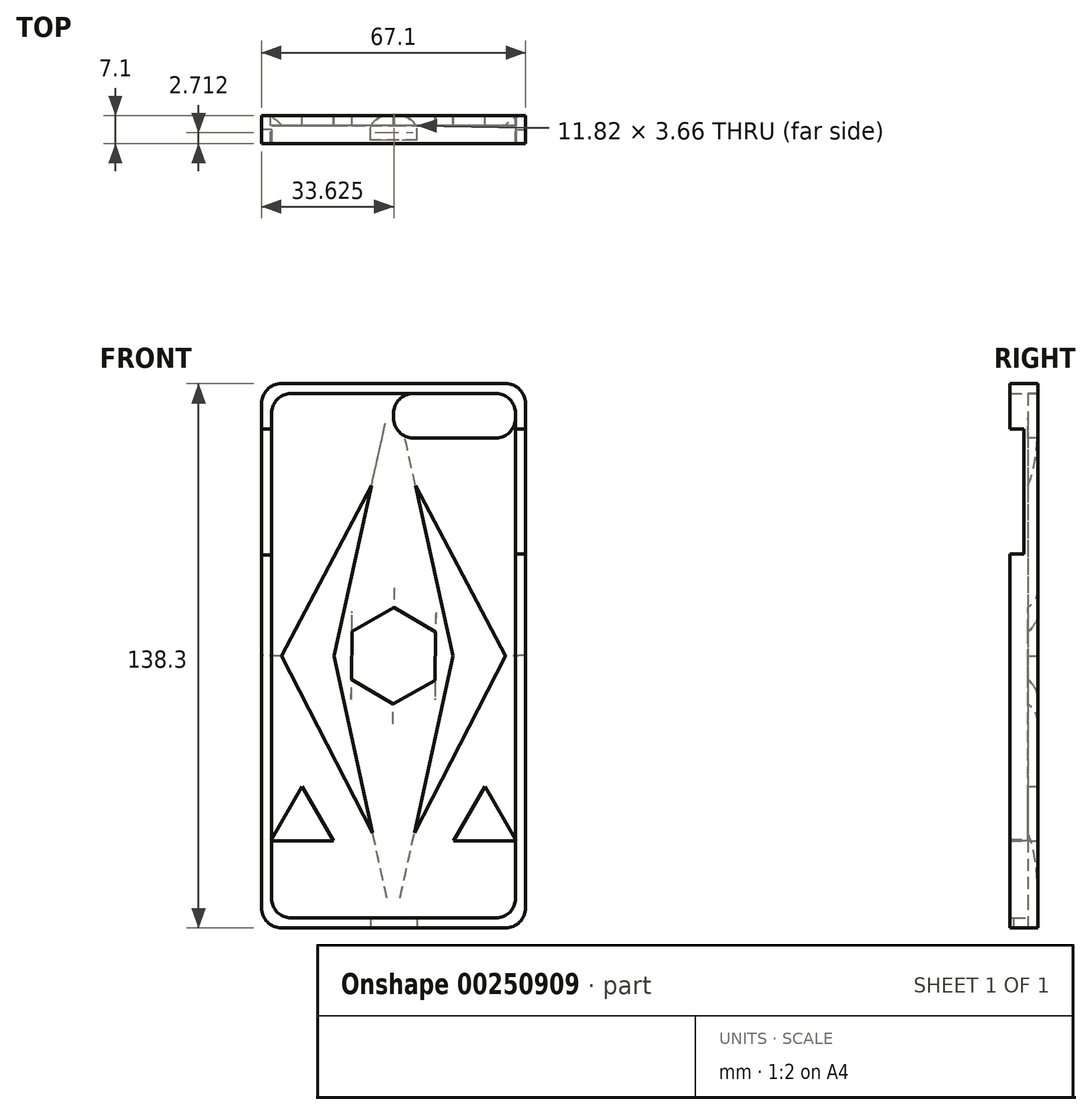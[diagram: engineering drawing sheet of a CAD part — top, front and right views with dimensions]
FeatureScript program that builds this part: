
annotation { "Feature Type Name" : "Feature", "Feature Type Description" : "" }
export const myFeature = defineFeature(function(context is Context, id is Id, definition is map)
    precondition{}
    {
        {
            var Q0;
            Q0=qCreatedBy(makeId("Front.planeOp"),FACE);
            var sketch = newSketch(context, id + "F0", { "sketchPlane" : qUnion([Q0])});
            skLineSegment(sketch, "E0.bottom", {"start": v(33.55, 69.15) * mm, "end": v(-33.55, 69.15) * mm});
            skLineSegment(sketch, "E0.top", {"start": v(33.55, -69.15) * mm, "end": v(-33.55, -69.15) * mm});
            skLineSegment(sketch, "E0.left", {"start": v(33.55, 69.15) * mm, "end": v(33.55, -69.15) * mm});
            skLineSegment(sketch, "E0.right", {"start": v(-33.55, 69.15) * mm, "end": v(-33.55, -69.15) * mm});
            skPoint(sketch, "E0.middle", {"position": v(0, 0) * mm});
            skSolve(sketch);
        }
        {
            var Q0;
            Q0=makeQuery(id+"F0.imprint","IMPRINT",FACE,{"disambiguationData":[TD([[makeQuery(id+"F0.imprint","IMPRINT",EDGE,{"derivedFrom":sQuery(id+"F0.wireOp",EDGE,"E0.bottom")}),1.0]])]});
            var Q1;
            Q1=sQuery(id+"F0.wireOp",EDGE,"E0.bottom");
            extrude(context, id + "F1", {"entities" : qUnion([Q0]), "surfaceEntities" : qUnion([Q1]), "endBound" : BoundingType.SYMMETRIC, "depth" : 7.1 * mm});
        }
        {
            var Q0;
            Q0=makeQuery(id+"F1.opExtrude","CAP_FACE",FACE,{"disambiguationData":[OSD([sQuery(id+"F0.wireOp",EDGE,"E0.bottom"),sQuery(id+"F0.wireOp",EDGE,"E0.top"),sQuery(id+"F0.wireOp",EDGE,"E0.left"),sQuery(id+"F0.wireOp",EDGE,"E0.right")])],"isStart":false});
            var Q1;
            Q1=makeQuery(id+"F1.opExtrude","SWEPT_BODY",BODY,{"disambiguationData":[OSD([sQuery(id+"F0.wireOp",EDGE,"E0.bottom"),sQuery(id+"F0.wireOp",EDGE,"E0.top"),sQuery(id+"F0.wireOp",EDGE,"E0.left"),sQuery(id+"F0.wireOp",EDGE,"E0.right")])]});
            shell(context, id + "F2", {"entities" : qUnion([Q0]), "parts" : qUnion([Q1]), "thickness" : 2.54 * mm});
        }
        {
            var Q0;
            Q0=makeQuery(id+"F1.opExtrude","SWEPT_EDGE",EDGE,{"disambiguationData":[OSD([sQuery(id+"F0.wireOp",EDGE,"E0.bottom"),sQuery(id+"F0.wireOp",EDGE,"E0.right")])]});
            var Q1;
            Q1=makeQuery(id+"F1.opExtrude","SWEPT_EDGE",EDGE,{"disambiguationData":[OSD([sQuery(id+"F0.wireOp",EDGE,"E0.bottom"),sQuery(id+"F0.wireOp",EDGE,"E0.left")])]});
            var Q2;
            Q2=makeQuery(id+"F1.opExtrude","SWEPT_EDGE",EDGE,{"disambiguationData":[OSD([sQuery(id+"F0.wireOp",EDGE,"E0.top"),sQuery(id+"F0.wireOp",EDGE,"E0.left")])]});
            var Q3;
            Q3=makeQuery(id+"F1.opExtrude","SWEPT_EDGE",EDGE,{"disambiguationData":[OSD([sQuery(id+"F0.wireOp",EDGE,"E0.top"),sQuery(id+"F0.wireOp",EDGE,"E0.right")])]});
            fillet(context, id + "F3", {"entities" : qUnion([Q0, Q1, Q2, Q3]), "radius" : 5.08 * mm, "tangentPropagation" : true, "allowEdgeOverflow" : false});
        }
        {
            var Q0;
            Q0=makeQuery(id+"F2.opShell","OFFSET_FACE",FACE,{"disambiguationData":[OSD([sQuery(id+"F0.wireOp",EDGE,"E0.bottom"),sQuery(id+"F0.wireOp",EDGE,"E0.top"),sQuery(id+"F0.wireOp",EDGE,"E0.left"),sQuery(id+"F0.wireOp",EDGE,"E0.right")])]});
            var sketch = newSketch(context, id + "F4", { "sketchPlane" : qUnion([Q0])});
            skLineSegment(sketch, "E1.bottom", {"start": v(33.35, 66.61) * mm, "end": v(0, 66.61) * mm});
            skLineSegment(sketch, "E1.top", {"start": v(33.35, 55.36) * mm, "end": v(0, 55.36) * mm});
            skLineSegment(sketch, "E1.left", {"start": v(33.35, 66.61) * mm, "end": v(33.35, 55.36) * mm});
            skLineSegment(sketch, "E1.right", {"start": v(0, 66.61) * mm, "end": v(0, 55.36) * mm});
            skSolve(sketch);
        }
        {
            var Q0;
            {var subQ4=sQuery(id+"F4.wireOp",EDGE,"E1.right");Q0=makeQuery(id+"F4.imprint","IMPRINT",FACE,{"disambiguationData":[TD([[makeQuery(id+"F4.imprint","IMPRINT",EDGE,{"derivedFrom":subQ4}),1.0]])]});}
            extrude(context, id + "F5", {"entities" : qUnion([Q0]), "operationType" : NewBodyOperationType.REMOVE, "endBound" : BoundingType.SYMMETRIC, "oppositeDirection" : true, "depth" : 25 * mm});
        }
        {
            var Q0;
            Q0=makeQuery(id+"F1.opExtrude","SWEPT_FACE",FACE,{"disambiguationData":[OSD([sQuery(id+"F0.wireOp",EDGE,"E0.top")])]});
            var sketch = newSketch(context, id + "F6", { "sketchPlane" : qUnion([Q0])});
            skLineSegment(sketch, "E2.bottom", {"start": v(5.99, 2.67) * mm, "end": v(-5.84, 2.67) * mm});
            skLineSegment(sketch, "E2.top", {"start": v(5.99, -1) * mm, "end": v(-5.84, -1) * mm});
            skLineSegment(sketch, "E2.left", {"start": v(5.99, 2.67) * mm, "end": v(5.99, -1) * mm});
            skLineSegment(sketch, "E2.right", {"start": v(-5.84, 2.67) * mm, "end": v(-5.84, -1) * mm});
            skSolve(sketch);
        }
        {
            var Q0;
            Q0=makeQuery(id+"F6.imprint","IMPRINT",FACE,{"disambiguationData":[TD([[makeQuery(id+"F6.imprint","IMPRINT",EDGE,{"derivedFrom":sQuery(id+"F6.wireOp",EDGE,"E2.bottom")}),1.0]])]});
            extrude(context, id + "F7", {"entities" : qUnion([Q0]), "operationType" : NewBodyOperationType.REMOVE, "endBound" : BoundingType.SYMMETRIC, "oppositeDirection" : true, "depth" : 25 * mm});
        }
        {
            var Q0;
            {var subQ0=sQuery(id+"F0.wireOp",EDGE,"E0.left");Q0=makeQuery(id+"F5.boolean.opBoolean","MERGE",EDGE,{"derivedFrom":[makeQuery(id+"F2.opShell","OFFSET_EDGE",EDGE,{"disambiguationData":[OSD([sQuery(id+"F0.wireOp",EDGE,"E0.bottom"),subQ0])]}),makeQuery(id+"F5.opExtrude","SWEPT_EDGE",EDGE,{"disambiguationData":[OSD([subQ0,sQuery(id+"F4.wireOp",EDGE,"E1.bottom")])]})]});}
            var Q1;
            Q1=makeQuery(id+"F5.boolean.opBoolean","COPY",EDGE,{"derivedFrom":makeQuery(id+"F5.opExtrude","SWEPT_EDGE",EDGE,{"disambiguationData":[OSD([sQuery(id+"F0.wireOp",EDGE,"E0.bottom"),sQuery(id+"F4.wireOp",EDGE,"E1.bottom"),sQuery(id+"F4.wireOp",EDGE,"E1.right")])]})});
            var Q2;
            Q2=makeQuery(id+"F5.boolean.opBoolean","COPY",EDGE,{"derivedFrom":makeQuery(id+"F5.opExtrude","SWEPT_EDGE",EDGE,{"disambiguationData":[OSD([sQuery(id+"F0.wireOp",EDGE,"E0.left"),sQuery(id+"F4.wireOp",EDGE,"E1.top")])]})});
            var Q3;
            Q3=makeQuery(id+"F5.boolean.opBoolean","COPY",EDGE,{"derivedFrom":makeQuery(id+"F5.opExtrude","SWEPT_EDGE",EDGE,{"disambiguationData":[OSD([sQuery(id+"F4.wireOp",EDGE,"E1.top"),sQuery(id+"F4.wireOp",EDGE,"E1.right")])]})});
            fillet(context, id + "F8", {"entities" : qUnion([Q0, Q1, Q2, Q3]), "radius" : 5 * mm, "tangentPropagation" : true, "allowEdgeOverflow" : false});
        }
        {
            var Q0;
            Q0=makeQuery(id+"F1.opExtrude","SWEPT_FACE",FACE,{"disambiguationData":[OSD([sQuery(id+"F0.wireOp",EDGE,"E0.right")])]});
            var sketch = newSketch(context, id + "F9", { "sketchPlane" : qUnion([Q0])});
            skLineSegment(sketch, "E3.bottom", {"start": v(3.55, 57.57) * mm, "end": v(0, 57.57) * mm});
            skLineSegment(sketch, "E3.top", {"start": v(3.55, 25.65) * mm, "end": v(0, 25.65) * mm});
            skLineSegment(sketch, "E3.left", {"start": v(3.55, 57.57) * mm, "end": v(3.55, 25.65) * mm});
            skLineSegment(sketch, "E3.right", {"start": v(0, 57.57) * mm, "end": v(0, 25.65) * mm});
            skSolve(sketch);
        }
        {
            var Q0;
            Q0=makeQuery(id+"F9.imprint","IMPRINT",FACE,{"disambiguationData":[TD([[makeQuery(id+"F9.imprint","IMPRINT",EDGE,{"derivedFrom":sQuery(id+"F9.wireOp",EDGE,"E3.bottom")}),1.0]])]});
            extrude(context, id + "F10", {"entities" : qUnion([Q0]), "operationType" : NewBodyOperationType.REMOVE, "endBound" : BoundingType.SYMMETRIC, "oppositeDirection" : true, "depth" : 25 * mm});
        }
        {
            var Q0;
            Q0=makeQuery(id+"F1.opExtrude","SWEPT_FACE",FACE,{"disambiguationData":[OSD([sQuery(id+"F0.wireOp",EDGE,"E0.left")])]});
            var sketch = newSketch(context, id + "F11", { "sketchPlane" : qUnion([Q0])});
            skLineSegment(sketch, "E4.bottom", {"start": v(-3.55, 57.64) * mm, "end": v(0, 57.64) * mm});
            skLineSegment(sketch, "E4.top", {"start": v(-3.55, 25.81) * mm, "end": v(0, 25.81) * mm});
            skLineSegment(sketch, "E4.left", {"start": v(-3.55, 57.64) * mm, "end": v(-3.55, 25.81) * mm});
            skLineSegment(sketch, "E4.right", {"start": v(0, 57.64) * mm, "end": v(0, 25.81) * mm});
            skSolve(sketch);
        }
        {
            var Q0;
            Q0=makeQuery(id+"F2.opShell","OFFSET_EDGE",EDGE,{"disambiguationData":[OSD([sQuery(id+"F0.wireOp",EDGE,"E0.top"),sQuery(id+"F0.wireOp",EDGE,"E0.right")])]});
            var Q1;
            Q1=makeQuery(id+"F2.opShell","OFFSET_EDGE",EDGE,{"disambiguationData":[OSD([sQuery(id+"F0.wireOp",EDGE,"E0.top"),sQuery(id+"F0.wireOp",EDGE,"E0.left")])]});
            var Q2;
            Q2=makeQuery(id+"F2.opShell","OFFSET_EDGE",EDGE,{"disambiguationData":[OSD([sQuery(id+"F0.wireOp",EDGE,"E0.bottom"),sQuery(id+"F0.wireOp",EDGE,"E0.right")])]});
            fillet(context, id + "F12", {"entities" : qUnion([Q0, Q1, Q2]), "radius" : 5 * mm, "tangentPropagation" : true, "allowEdgeOverflow" : false});
        }
        {
            var Q0;
            Q0 = qSketchRegion(id + "F11", true);
            extrude(context, id + "F13", {"entities" : qUnion([Q0]), "operationType" : NewBodyOperationType.REMOVE, "endBound" : BoundingType.SYMMETRIC, "oppositeDirection" : true, "depth" : 25 * mm});
        }
        {
            var Q0;
            Q0=makeQuery(id+"F1.opExtrude","CAP_FACE",FACE,{"disambiguationData":[OSD([sQuery(id+"F0.wireOp",EDGE,"E0.bottom"),sQuery(id+"F0.wireOp",EDGE,"E0.top"),sQuery(id+"F0.wireOp",EDGE,"E0.left"),sQuery(id+"F0.wireOp",EDGE,"E0.right")])],"isStart":true});
            var sketch = newSketch(context, id + "F14", { "sketchPlane" : qUnion([Q0])});
            skLineSegment(sketch, "E5", {"start": v(-5.58, 43.21) * mm, "end": v(-15.13, 0) * mm});
            skLineSegment(sketch, "E6", {"start": v(-15.13, 0) * mm, "end": v(-5.3, -44.99) * mm});
            skLineSegment(sketch, "E7", {"start": v(-5.3, -44.99) * mm, "end": v(-28.47, 0) * mm});
            skLineSegment(sketch, "E8", {"start": v(-28.47, 0) * mm, "end": v(-5.58, 43.21) * mm});
            skLineSegment(sketch, "E9.MirrorCS", {"start": v(5.58, 43.21) * mm, "end": v(15.13, 0) * mm});
            skLineSegment(sketch, "E10.MirrorCS", {"start": v(28.47, 0) * mm, "end": v(5.58, 43.21) * mm});
            skLineSegment(sketch, "E11.MirrorCS", {"start": v(15.13, 0) * mm, "end": v(5.3, -44.99) * mm});
            skLineSegment(sketch, "E12.MirrorCS", {"start": v(5.3, -44.99) * mm, "end": v(28.47, 0) * mm});
            skSolve(sketch);
        }
        {
            var Q0;
            Q0=makeQuery(id+"F14.imprint","IMPRINT",FACE,{"disambiguationData":[TD([[makeQuery(id+"F14.imprint","IMPRINT",EDGE,{"derivedFrom":sQuery(id+"F14.wireOp",EDGE,"E5")}),-1.0]])]});
            var Q1;
            Q1=makeQuery(id+"F14.imprint","IMPRINT",FACE,{"disambiguationData":[TD([[makeQuery(id+"F14.imprint","IMPRINT",EDGE,{"derivedFrom":sQuery(id+"F14.wireOp",EDGE,"E9.MirrorCS")}),1.0]])]});
            extrude(context, id + "F15", {"entities" : qUnion([Q0, Q1]), "operationType" : NewBodyOperationType.REMOVE, "endBound" : BoundingType.SYMMETRIC, "oppositeDirection" : true, "depth" : 25 * mm});
        }
        {
            var Q0;
            Q0=makeQuery(id+"F1.opExtrude","CAP_FACE",FACE,{"disambiguationData":[OSD([sQuery(id+"F0.wireOp",EDGE,"E0.bottom"),sQuery(id+"F0.wireOp",EDGE,"E0.top"),sQuery(id+"F0.wireOp",EDGE,"E0.left"),sQuery(id+"F0.wireOp",EDGE,"E0.right")])],"isStart":true});
            var sketch = newSketch(context, id + "F16", { "sketchPlane" : qUnion([Q0])});
            skCircle(sketch, "E13.cCircle", {"center": v(0, 0) * mm, "radius": 10.61 * mm, "construction": true});
            skLineSegment(sketch, "E13.0", {"start": v(10.68, -6.01) * mm, "end": v(0.13, -12.25) * mm});
            skLineSegment(sketch, "E13.1", {"start": v(0.13, -12.25) * mm, "end": v(-10.54, -6.24) * mm});
            skLineSegment(sketch, "E13.2", {"start": v(-10.54, -6.24) * mm, "end": v(-10.68, 6.01) * mm});
            skLineSegment(sketch, "E13.3", {"start": v(-10.68, 6.01) * mm, "end": v(-0.13, 12.25) * mm});
            skLineSegment(sketch, "E13.4", {"start": v(-0.13, 12.25) * mm, "end": v(10.54, 6.24) * mm});
            skLineSegment(sketch, "E13.5", {"start": v(10.54, 6.24) * mm, "end": v(10.68, -6.01) * mm});
            skPoint(sketch, "E13.0.midPoint", {"position": v(5.4, -9.13) * mm});
            skCircle(sketch, "E14.cCircle", {"center": v(-23.22, -42.39) * mm, "radius": 4.63 * mm, "construction": true});
            skLineSegment(sketch, "E14.0", {"start": v(-15.21, -47.01) * mm, "end": v(-31.24, -47.01) * mm});
            skLineSegment(sketch, "E14.1", {"start": v(-31.24, -47.01) * mm, "end": v(-23.22, -33.13) * mm});
            skLineSegment(sketch, "E14.2", {"start": v(-23.22, -33.13) * mm, "end": v(-15.21, -47.01) * mm});
            skPoint(sketch, "E14.0.midPoint", {"position": v(-23.22, -47.01) * mm});
            skLineSegment(sketch, "E15.MirrorCS", {"start": v(31.24, -47.01) * mm, "end": v(23.22, -33.13) * mm});
            skLineSegment(sketch, "E16.MirrorCS", {"start": v(23.22, -33.13) * mm, "end": v(15.21, -47.01) * mm});
            skLineSegment(sketch, "E17.MirrorCS", {"start": v(15.21, -47.01) * mm, "end": v(31.24, -47.01) * mm});
            skCircle(sketch, "E18.MirrorC", {"center": v(23.22, -42.39) * mm, "radius": 4.63 * mm, "construction": true});
            skSolve(sketch);
        }
        {
            var Q0;
            Q0=makeQuery(id+"F16.imprint","IMPRINT",FACE,{"disambiguationData":[TD([[makeQuery(id+"F16.imprint","IMPRINT",EDGE,{"derivedFrom":sQuery(id+"F16.wireOp",EDGE,"E14.0")}),-1.0]])]});
            var Q1;
            Q1=makeQuery(id+"F16.imprint","IMPRINT",FACE,{"disambiguationData":[TD([[makeQuery(id+"F16.imprint","IMPRINT",EDGE,{"derivedFrom":sQuery(id+"F16.wireOp",EDGE,"E15.MirrorCS")}),1.0]])]});
            var Q2;
            Q2=makeQuery(id+"F16.imprint","IMPRINT",FACE,{"disambiguationData":[TD([[makeQuery(id+"F16.imprint","IMPRINT",EDGE,{"derivedFrom":sQuery(id+"F16.wireOp",EDGE,"E13.0")}),-1.0]])]});
            extrude(context, id + "F17", {"entities" : qUnion([Q0, Q1, Q2]), "operationType" : NewBodyOperationType.REMOVE, "endBound" : BoundingType.SYMMETRIC, "oppositeDirection" : true, "depth" : 25 * mm});
        }
        {
            var Q0;
            Q0=makeQuery(id+"F15.boolean.opBoolean","INTERSECT",EDGE,{"derivedFrom":[makeQuery(id+"F1.opExtrude","CAP_FACE",FACE,{"disambiguationData":[OSD([sQuery(id+"F0.wireOp",EDGE,"E0.bottom"),sQuery(id+"F0.wireOp",EDGE,"E0.top"),sQuery(id+"F0.wireOp",EDGE,"E0.left"),sQuery(id+"F0.wireOp",EDGE,"E0.right")])],"isStart":true}),makeQuery(id+"F15.opExtrude","SWEPT_FACE",FACE,{"disambiguationData":[OSD([sQuery(id+"F14.wireOp",EDGE,"E8")])]})]});
            var Q1;
            Q1=makeQuery(id+"F15.boolean.opBoolean","INTERSECT",EDGE,{"derivedFrom":[makeQuery(id+"F1.opExtrude","CAP_FACE",FACE,{"disambiguationData":[OSD([sQuery(id+"F0.wireOp",EDGE,"E0.bottom"),sQuery(id+"F0.wireOp",EDGE,"E0.top"),sQuery(id+"F0.wireOp",EDGE,"E0.left"),sQuery(id+"F0.wireOp",EDGE,"E0.right")])],"isStart":true}),makeQuery(id+"F15.opExtrude","SWEPT_FACE",FACE,{"disambiguationData":[OSD([sQuery(id+"F14.wireOp",EDGE,"E7")])]})]});
            var Q2;
            Q2=makeQuery(id+"F15.boolean.opBoolean","INTERSECT",EDGE,{"derivedFrom":[makeQuery(id+"F1.opExtrude","CAP_FACE",FACE,{"disambiguationData":[OSD([sQuery(id+"F0.wireOp",EDGE,"E0.bottom"),sQuery(id+"F0.wireOp",EDGE,"E0.top"),sQuery(id+"F0.wireOp",EDGE,"E0.left"),sQuery(id+"F0.wireOp",EDGE,"E0.right")])],"isStart":true}),makeQuery(id+"F15.opExtrude","SWEPT_FACE",FACE,{"disambiguationData":[OSD([sQuery(id+"F14.wireOp",EDGE,"E10.MirrorCS")])]})]});
            var Q3;
            Q3=makeQuery(id+"F15.boolean.opBoolean","INTERSECT",EDGE,{"derivedFrom":[makeQuery(id+"F1.opExtrude","CAP_FACE",FACE,{"disambiguationData":[OSD([sQuery(id+"F0.wireOp",EDGE,"E0.bottom"),sQuery(id+"F0.wireOp",EDGE,"E0.top"),sQuery(id+"F0.wireOp",EDGE,"E0.left"),sQuery(id+"F0.wireOp",EDGE,"E0.right")])],"isStart":true}),makeQuery(id+"F15.opExtrude","SWEPT_FACE",FACE,{"disambiguationData":[OSD([sQuery(id+"F14.wireOp",EDGE,"E12.MirrorCS")])]})]});
            var Q4;
            Q4=makeQuery(id+"F17.boolean.opBoolean","INTERSECT",EDGE,{"derivedFrom":[makeQuery(id+"F1.opExtrude","CAP_FACE",FACE,{"disambiguationData":[OSD([sQuery(id+"F0.wireOp",EDGE,"E0.bottom"),sQuery(id+"F0.wireOp",EDGE,"E0.top"),sQuery(id+"F0.wireOp",EDGE,"E0.left"),sQuery(id+"F0.wireOp",EDGE,"E0.right")])],"isStart":true}),makeQuery(id+"F17.opExtrude","SWEPT_FACE",FACE,{"disambiguationData":[OSD([sQuery(id+"F16.wireOp",EDGE,"E13.3")])]})]});
            var Q5;
            Q5=makeQuery(id+"F17.boolean.opBoolean","INTERSECT",EDGE,{"derivedFrom":[makeQuery(id+"F1.opExtrude","CAP_FACE",FACE,{"disambiguationData":[OSD([sQuery(id+"F0.wireOp",EDGE,"E0.bottom"),sQuery(id+"F0.wireOp",EDGE,"E0.top"),sQuery(id+"F0.wireOp",EDGE,"E0.left"),sQuery(id+"F0.wireOp",EDGE,"E0.right")])],"isStart":true}),makeQuery(id+"F17.opExtrude","SWEPT_FACE",FACE,{"disambiguationData":[OSD([sQuery(id+"F16.wireOp",EDGE,"E13.4")])]})]});
            var Q6;
            Q6=makeQuery(id+"F17.boolean.opBoolean","INTERSECT",EDGE,{"derivedFrom":[makeQuery(id+"F1.opExtrude","CAP_FACE",FACE,{"disambiguationData":[OSD([sQuery(id+"F0.wireOp",EDGE,"E0.bottom"),sQuery(id+"F0.wireOp",EDGE,"E0.top"),sQuery(id+"F0.wireOp",EDGE,"E0.left"),sQuery(id+"F0.wireOp",EDGE,"E0.right")])],"isStart":true}),makeQuery(id+"F17.opExtrude","SWEPT_FACE",FACE,{"disambiguationData":[OSD([sQuery(id+"F16.wireOp",EDGE,"E13.1")])]})]});
            var Q7;
            Q7=makeQuery(id+"F17.boolean.opBoolean","INTERSECT",EDGE,{"derivedFrom":[makeQuery(id+"F1.opExtrude","CAP_FACE",FACE,{"disambiguationData":[OSD([sQuery(id+"F0.wireOp",EDGE,"E0.bottom"),sQuery(id+"F0.wireOp",EDGE,"E0.top"),sQuery(id+"F0.wireOp",EDGE,"E0.left"),sQuery(id+"F0.wireOp",EDGE,"E0.right")])],"isStart":true}),makeQuery(id+"F17.opExtrude","SWEPT_FACE",FACE,{"disambiguationData":[OSD([sQuery(id+"F16.wireOp",EDGE,"E13.0")])]})]});
            fillet(context, id + "F18", {"entities" : qUnion([Q0, Q1, Q2, Q3, Q4, Q5, Q6, Q7]), "radius" : 5 * mm, "tangentPropagation" : true, "allowEdgeOverflow" : false});
        }
    });
